# Revit family: RA 20
name_source: partatom
category: Lighting Fixtures
units: mm (PartAtom-declared; Revit-internal decimal feet)

## family parameters
Always vertical = Yes
Cut with Voids When Loaded = No
Host = Ceiling
Light Source = Yes
OmniClass Number = 23.80.70.11
OmniClass Title = Luminaries for Internal Lighting
Part Type = Normal
Room Calculation Point = No
Round Connector Dimension = Use Diameter
Shared = No

## types (2) — shared parameters
Beam angle (°) = 100°
Body material = White Powder Coated Aluminium
CRI L'indice di Resa Cromatica = 85
Color Filter = 16777215
Corrente driver (mA) = 1400mA
Default Elevation = 0 mm
Description = Incassi professionali fissi in grado di offrire elevate prestazioni illuminotecniche, grazie all’utilizzo di sorgenti LED COB di ultima generazione. 
Gli apparecchi RA 20 DIXIT LED, a dissipazione termica passiva, garantiscono un'elevata densità luminosa ed un'eccellente resa cromatica. Sono facilmente installabili con molle in controsoffitti da 1 a 30 mm.
LED driver da ordinare separatamente, la potenza dell'apparecchio varia a seconda del driver scelto.
Grado di protezione IP43.
Dimming Lamp Color Temperature Shift = <None>
Glass material = Glass
Larghezza = 200 mm
Manufacturer = ARIA
Model = 244-242
Tilt Angle = 90.00°
Type Comments = Ceiling recessed light
Type Image = RA20_DIXIT_LED_TAB-Sito-Ivela.jpg
URL = https://www.aria.lighting
Wattage Comments = 51

## per-type parameters (varying)
| type | Codice | Effective Intensity (lm) | Lamp | Photometric Web File |
| RA 20 Dixit LED 51W 3000K | 244-242BN-21 | 5485 | LED 6400lm 51W 3000K CRI85 | 244-24 _ 224-242DD _ RA 20 DIXIT LED 51W 6400 lm 100°.IES |
| RA 20 Dixit LED 51W 4000K | 244-242AN-21 | 5656 | LED 6600lm 51W 4000K CRI85 | 244-24 _ RA 20 DIXIT LED 51W 6600 lm 100° 4000K.IES |

## geometry (parser evidence)
native form markers: Sweep x3
no freeform markers — native parametric forms only
